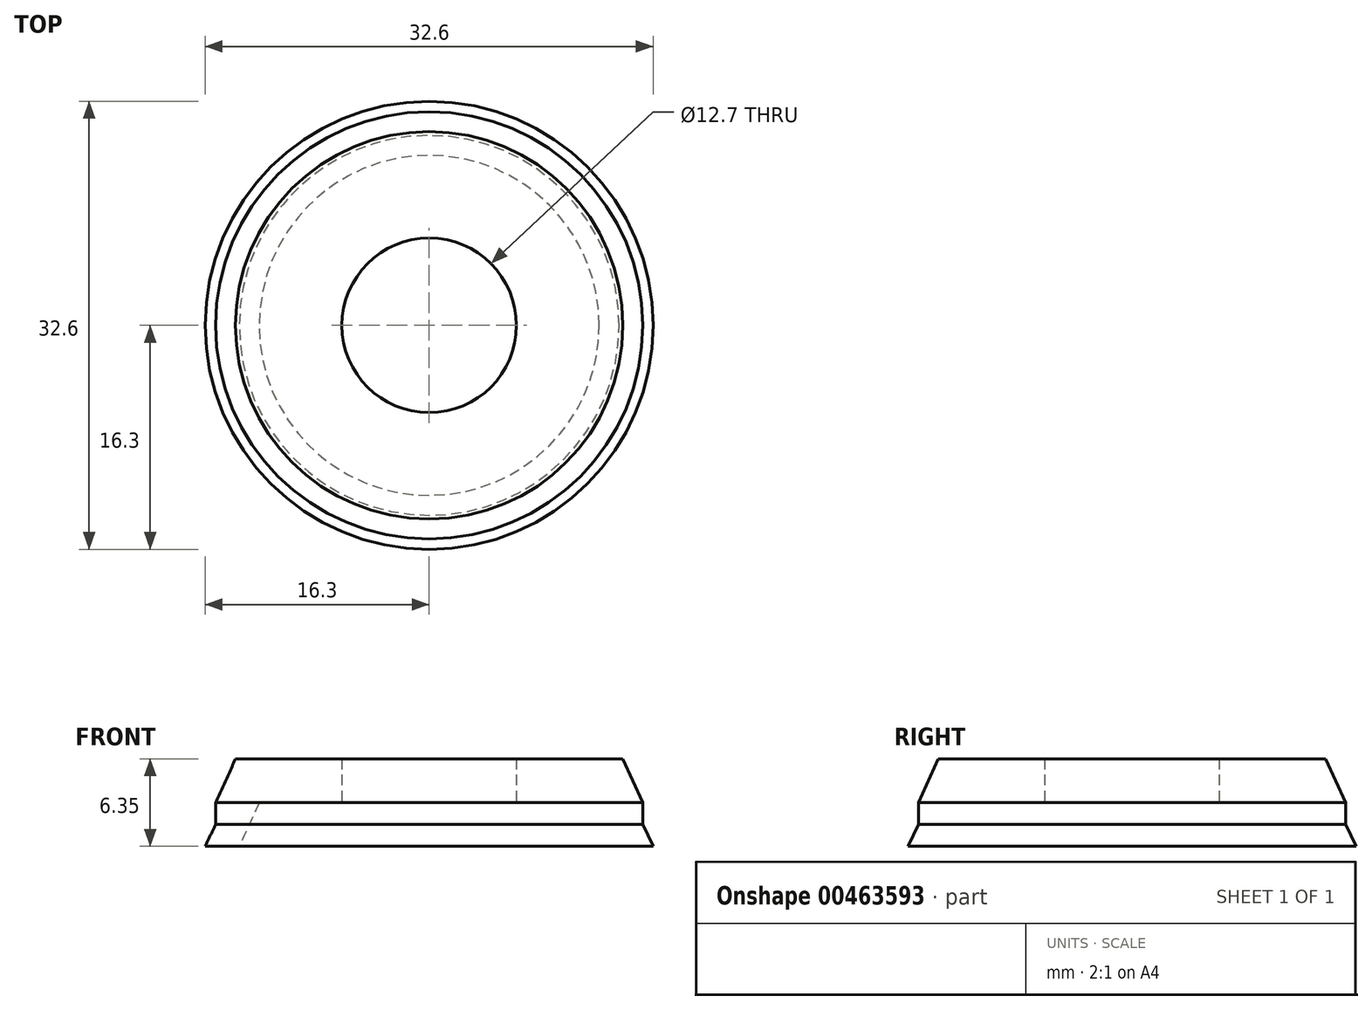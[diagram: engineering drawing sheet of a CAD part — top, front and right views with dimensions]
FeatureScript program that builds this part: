
annotation { "Feature Type Name" : "Feature", "Feature Type Description" : "" }
export const myFeature = defineFeature(function(context is Context, id is Id, definition is map)
    precondition{}
    {
        {
            var Q0;
            Q0=qCreatedBy(makeId("Front.planeOp"),FACE);
            var sketch = newSketch(context, id + "F0", { "sketchPlane" : qUnion([Q0])});
            skLineSegment(sketch, "E0", {"start": v(6.35, 3.18) * mm, "end": v(12.37, 3.18) * mm});
            skLineSegment(sketch, "E1", {"start": v(6.35, 3.18) * mm, "end": v(6.35, 6.35) * mm});
            skLineSegment(sketch, "E2", {"start": v(6.35, 6.35) * mm, "end": v(10.92, 6.35) * mm});
            skLineSegment(sketch, "E3", {"start": v(13.82, 0) * mm, "end": v(16.3, 0) * mm});
            skLineSegment(sketch, "E4", {"start": v(12.37, 3.18) * mm, "end": v(13.82, 0) * mm});
            skPoint(sketch, "E5.orphan", {"position": v(6.35, 0) * mm});
            skLineSegment(sketch, "E6", {"start": v(10.92, 6.35) * mm, "end": v(14.1, 6.35) * mm});
            skLineSegment(sketch, "E7", {"start": v(14.1, 6.35) * mm, "end": v(15.54, 3.18) * mm});
            skPoint(sketch, "E8.end.orphan", {"position": v(0, 3.18) * mm});
            skLineSegment(sketch, "E9", {"start": v(0, 0) * mm, "end": v(0, 6.96) * mm, "construction": true});
            skLineSegment(sketch, "E10", {"start": v(15.54, 3.18) * mm, "end": v(15.54, 1.59) * mm});
            skLineSegment(sketch, "E11", {"start": v(15.54, 1.59) * mm, "end": v(16.3, 0) * mm});
            skPoint(sketch, "E12.end.orphan", {"position": v(41.28, 0) * mm});
            skSolve(sketch);
        }
        {
            var Q0;
            Q0=makeQuery(id+"F0.imprint","IMPRINT",FACE,{"disambiguationData":[TD([[makeQuery(id+"F0.imprint","IMPRINT",EDGE,{"derivedFrom":sQuery(id+"F0.wireOp",EDGE,"E0")}),1.0]])]});
            var Q1;
            Q1=sQuery(id+"F0.wireOp",EDGE,"E9");
            revolve(context, id + "F1", {"entities" : qUnion([Q0]), "axis" : qUnion([Q1]), "revolveType" : RevolveType.FULL});
        }
    });
